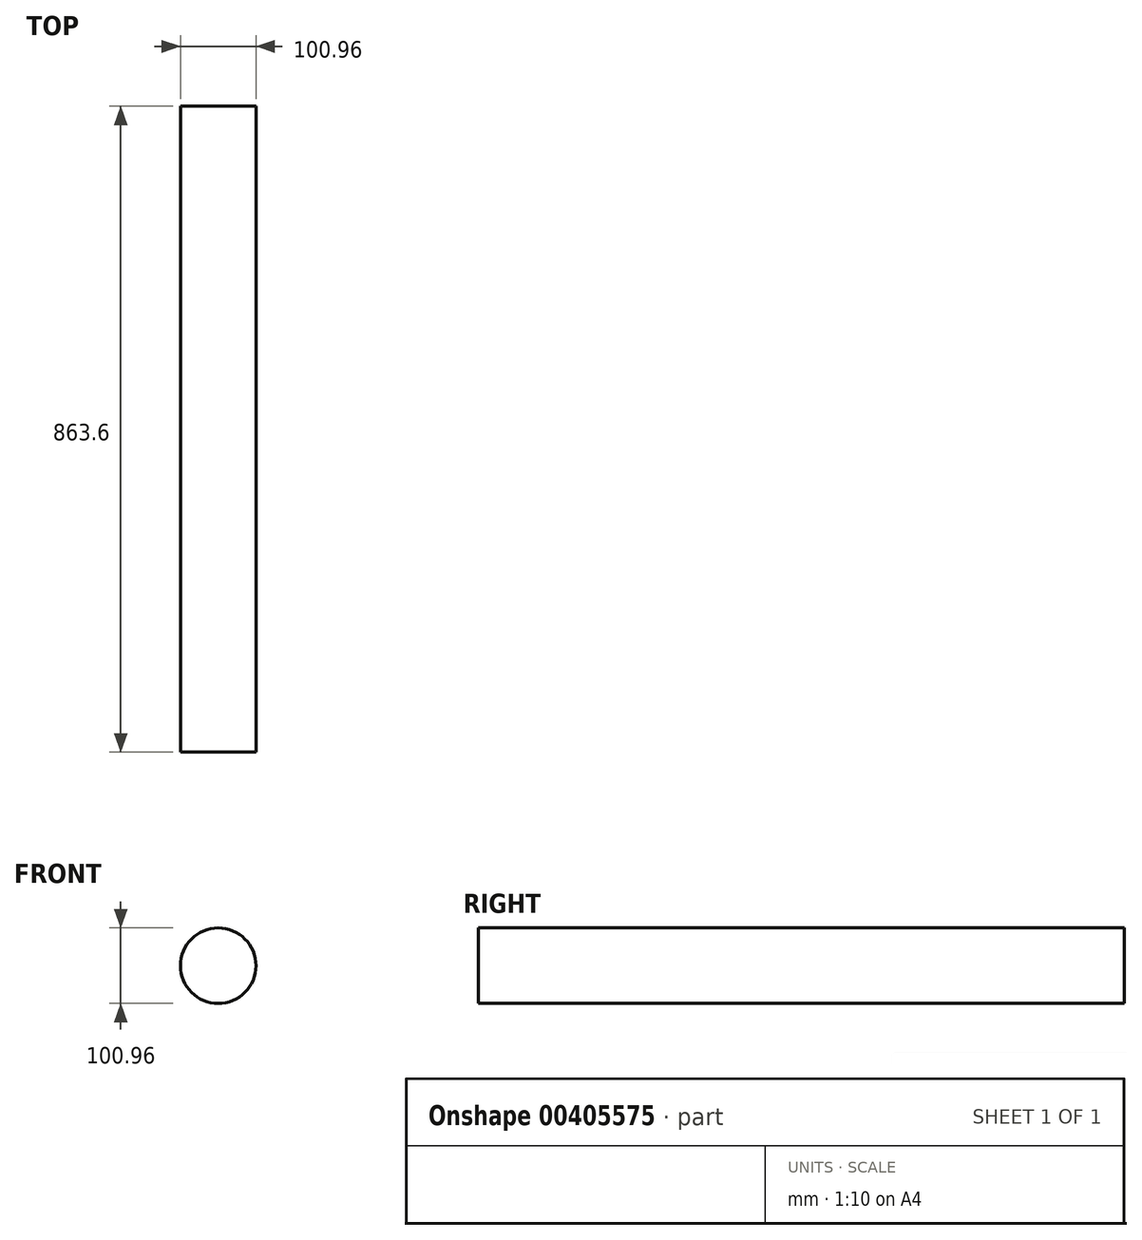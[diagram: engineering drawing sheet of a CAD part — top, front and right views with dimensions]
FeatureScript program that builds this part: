
annotation { "Feature Type Name" : "Feature", "Feature Type Description" : "" }
export const myFeature = defineFeature(function(context is Context, id is Id, definition is map)
    precondition{}
    {
        {
            var Q0;
            Q0=qCreatedBy(makeId("Front.planeOp"),FACE);
            var sketch = newSketch(context, id + "F0", { "sketchPlane" : qUnion([Q0])});
            skCircle(sketch, "E0", {"center": v(0, 0) * mm, "radius": 50.48 * mm});
            skSolve(sketch);
        }
        {
            var Q0;
            Q0=makeQuery(id+"F0.imprint","IMPRINT",FACE,{"disambiguationData":[TD([[makeQuery(id+"F0.imprint","IMPRINT",EDGE,{"derivedFrom":sQuery(id+"F0.wireOp",EDGE,"E0")}),1.0]])]});
            extrude(context, id + "F1", {"entities" : qUnion([Q0]), "depth" : 863.6 * mm});
        }
    });
